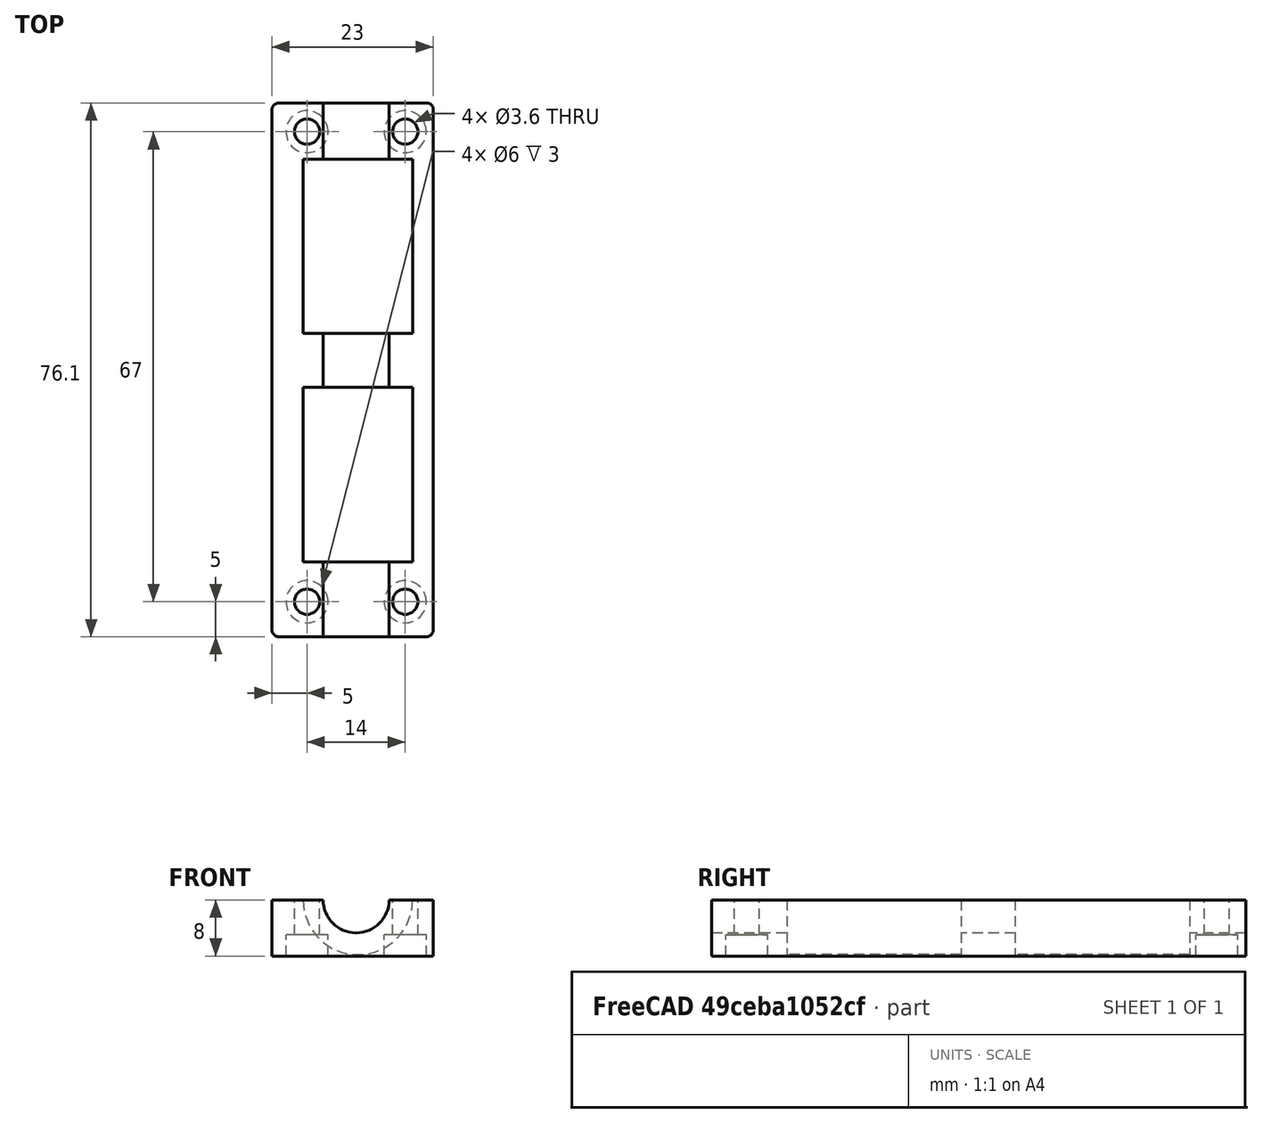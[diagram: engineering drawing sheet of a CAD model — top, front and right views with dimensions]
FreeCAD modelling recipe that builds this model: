
FCSTD DOCUMENT  (FreeCAD 0.16R6706 (Git))
Label: Carcasa 2 5.0
License: All rights reserved
LicenseURL: http://en.wikipedia.org/wiki/All_rights_reserved
objects: Part::Cylinder×12, Part::Cut×12, Part::Box×1, Part::Fillet×1
note: 26 computed .brp shape members not serialized (recipe doc carries the construction recipe); baked Part::Feature solids carry a one-line shape summary decoded from their .brp

FEATURE [Part::Cylinder] Cylinder048
  Angle = 360
  Height = 100
  Placement = pos=(12,79,0) rot=(1,0,0;1.5708rad)
  Radius = 4.7
FEATURE [Part::Box] Box011  label="Cubo007"
  Height = 8
  Length = 23
  Placement = pos=(0,0,-8) rot=(0,0,1;0rad)
  Width = 76.1
FEATURE [Part::Cylinder] Cylinder028  label="Rodamiento 009"
  Angle = 360
  Height = 24.85
  Placement = pos=(12.25,35.55,0) rot=(1,0,0;1.5708rad)
  Radius = 7.8
FEATURE [Part::Cylinder] Cylinder029  label="Rodamiento 010"
  Angle = 360
  Height = 24.85
  Placement = pos=(12.25,68.1,0) rot=(1,0,0;1.5708rad)
  Radius = 7.8
FEATURE [Part::Cylinder] Cylinder030  label="Eje 005"
  Angle = 360
  Height = 76.1
  Placement = pos=(12.25,76.1,0) rot=(1,0,0;1.5708rad)
  Radius = 4.4
FEATURE [Part::Cut] Cut010035003006
  Base = -> Box011
  Tool = -> Cylinder028
FEATURE [Part::Cut] Cut010035003007
  Base = -> Cut010035003006
  Tool = -> Cylinder030
FEATURE [Part::Cut] Cut010035003008
  Base = -> Cut010035003007
  Tool = -> Cylinder029
FEATURE [Part::Cylinder] Cylinder031  label="Cilindro016"
  Angle = 360
  Height = 20
  Placement = pos=(5,5,-10) rot=(0,0,1;0rad)
  Radius = 1.8
FEATURE [Part::Cylinder] Cylinder032  label="Cilindro017"
  Angle = 360
  Height = 20
  Placement = pos=(5,72,-10) rot=(0,0,1;0rad)
  Radius = 1.8
FEATURE [Part::Cut] Cut010035003009
  Base = -> Cut010035003008
  Tool = -> Cylinder032
FEATURE [Part::Cut] Cut010035003010
  Base = -> Cut010035003009
  Tool = -> Cylinder031
FEATURE [Part::Fillet] Fillet003002  label="Carcasa 005"
  Base = -> Cut010035003010
  Edges = 4 edges r=1: [Edge1,Edge3,Edge5,Edge22]
FEATURE [Part::Cylinder] Cylinder033  label="Cilindro018"
  Angle = 360
  Height = 10
  Placement = pos=(5,5,-15) rot=(0,0,1;0rad)
  Radius = 3
FEATURE [Part::Cylinder] Cylinder034  label="Cilindro019"
  Angle = 360
  Height = 10
  Placement = pos=(5,72,-15) rot=(0,0,1;0rad)
  Radius = 3
FEATURE [Part::Cut] Cut010035003011
  Base = -> Fillet003002
  Tool = -> Cylinder033
FEATURE [Part::Cut] Cut010035003012  label="Carcasa 2'"
  Base = -> Cut010035003011
  Tool = -> Cylinder034
FEATURE [Part::Cylinder] Cylinder041  label="Cilindro026"
  Angle = 360
  Height = 10
  Placement = pos=(19,72,-15) rot=(0,0,1;0rad)
  Radius = 3
FEATURE [Part::Cylinder] Cylinder042  label="Cilindro027"
  Angle = 360
  Height = 20
  Placement = pos=(19,72,-10) rot=(0,0,1;0rad)
  Radius = 1.8
FEATURE [Part::Cut] Cut010035003022
  Base = -> Cut010035003012
  Tool = -> Cylinder041
FEATURE [Part::Cut] Cut010035003023  label="Carcasa 2 '''"
  Base = -> Cut010035003022
  Tool = -> Cylinder042
FEATURE [Part::Cylinder] Cylinder044  label="Cilindro029"
  Angle = 360
  Height = 10
  Placement = pos=(19,5,-15) rot=(0,0,1;0rad)
  Radius = 3
FEATURE [Part::Cylinder] Cylinder045  label="Cilindro030"
  Angle = 360
  Height = 20
  Placement = pos=(19,5,-10) rot=(0,0,1;0rad)
  Radius = 1.8
FEATURE [Part::Cut] Cut010035003026
  Base = -> Cut010035003023
  Tool = -> Cylinder044
FEATURE [Part::Cut] Cut010035003027  label="Carcasa 2 V"
  Base = -> Cut010035003026
  Tool = -> Cylinder045
FEATURE [Part::Cut] Cut010035003032  label="Carcasa 2 VI"
  Base = -> Cut010035003027
  Tool = -> Cylinder048
